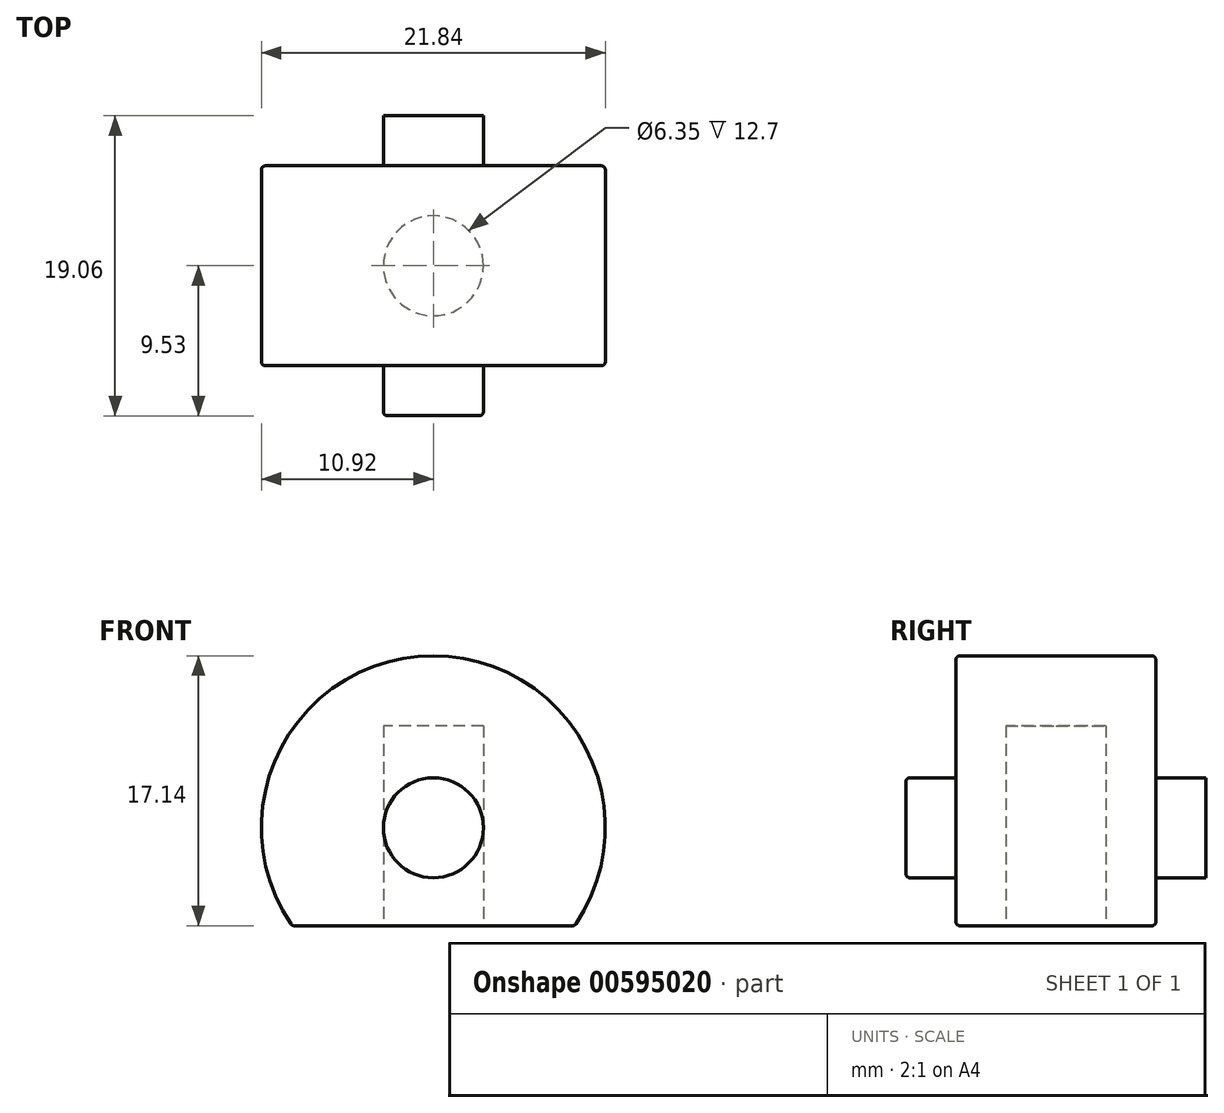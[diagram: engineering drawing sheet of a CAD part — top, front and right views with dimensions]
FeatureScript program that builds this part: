
annotation { "Feature Type Name" : "Feature", "Feature Type Description" : "" }
export const myFeature = defineFeature(function(context is Context, id is Id, definition is map)
    precondition{}
    {
        {
            var Q0;
            Q0=qCreatedBy(makeId("Front.planeOp"),FACE);
            var sketch = newSketch(context, id + "F0", { "sketchPlane" : qUnion([Q0])});
            skArc(sketch, "E0", {"start": v(8.98, 0) * mm, "mid": v(0, 17.14) * mm, "end": v(-8.98, 0) * mm});
            skLineSegment(sketch, "E1", {"start": v(-8.98, 0) * mm, "end": v(8.98, 0) * mm});
            skSolve(sketch);
        }
        {
            var Q0;
            Q0=qCreatedBy(makeId("Front.planeOp"),FACE);
            var sketch = newSketch(context, id + "F1", { "sketchPlane" : qUnion([Q0])});
            skCircle(sketch, "E2", {"center": v(0, 6.22) * mm, "radius": 3.18 * mm});
            skSolve(sketch);
        }
        {
            var Q0;
            Q0=qCreatedBy(makeId("Top.planeOp"),FACE);
            var sketch = newSketch(context, id + "F2", { "sketchPlane" : qUnion([Q0])});
            skCircle(sketch, "E3", {"center": v(0, 0) * mm, "radius": 3.18 * mm});
            skSolve(sketch);
        }
        {
            var Q0;
            Q0 = qSketchRegion(id + "F0", true);
            extrude(context, id + "F3", {"entities" : qUnion([Q0]), "endBound" : BoundingType.SYMMETRIC, "depth" : 12.7 * mm, "offsetDistance" : 25.4 * mm});
        }
        {
            var Q0;
            Q0 = qSketchRegion(id + "F1", true);
            extrude(context, id + "F4", {"entities" : qUnion([Q0]), "operationType" : NewBodyOperationType.ADD, "endBound" : BoundingType.SYMMETRIC, "depth" : 19.05 * mm, "offsetDistance" : 25.4 * mm});
        }
        {
            var Q0;
            Q0 = qSketchRegion(id + "F2", true);
            extrude(context, id + "F5", {"entities" : qUnion([Q0]), "operationType" : NewBodyOperationType.REMOVE, "depth" : 12.7 * mm, "offsetDistance" : 25.4 * mm});
        }
        {
            var Q0;
            Q0=makeQuery(id+"F3.opExtrude","CAP_EDGE",EDGE,{"disambiguationData":[OSD([sQuery(id+"F0.wireOp",EDGE,"E0")])],"isStart":false});
            var Q1;
            Q1=makeQuery(id+"F3.opExtrude","CAP_EDGE",EDGE,{"disambiguationData":[OSD([sQuery(id+"F0.wireOp",EDGE,"E0")])],"isStart":true});
            var Q2;
            {var subQ0=sQuery(id+"F0.wireOp",EDGE,"E1");var subQ1=sQuery(id+"F0.wireOp",EDGE,"E0");Q2=makeQuery(id+"F3.opExtrude","SWEPT_EDGE",EDGE,{"disambiguationData":[OSD([subQ1,subQ0]),TDD([makeQuery(id+"F0.imprint","INTERSECT",VERTEX,{"disambiguationData":[OD(0.0)],"derivedFrom":[subQ1,subQ0]})])]});}
            var Q3;
            Q3=makeQuery(id+"F3.opExtrude","CAP_EDGE",EDGE,{"disambiguationData":[OSD([sQuery(id+"F0.wireOp",EDGE,"E1")])],"isStart":false});
            var Q4;
            Q4=makeQuery(id+"F4.opExtrude","CAP_EDGE",EDGE,{"disambiguationData":[OSD([sQuery(id+"F1.wireOp",EDGE,"E2")])],"isStart":false});
            var Q5;
            Q5=makeQuery(id+"F3.opExtrude","CAP_EDGE",EDGE,{"disambiguationData":[OSD([sQuery(id+"F0.wireOp",EDGE,"E1")])],"isStart":true});
            var Q6;
            {var subQ0=sQuery(id+"F0.wireOp",EDGE,"E1");var subQ1=sQuery(id+"F0.wireOp",EDGE,"E0");Q6=makeQuery(id+"F3.opExtrude","SWEPT_EDGE",EDGE,{"disambiguationData":[OSD([subQ1,subQ0]),TDD([makeQuery(id+"F0.imprint","INTERSECT",VERTEX,{"disambiguationData":[OD(1.0)],"derivedFrom":[subQ1,subQ0]})])]});}
            fillet(context, id + "F6", {"entities" : qUnion([Q0, Q1, Q2, Q3, Q4, Q5, Q6]), "radius" : 0.25 * mm, "tangentPropagation" : true, "allowEdgeOverflow" : false});
        }
    });
